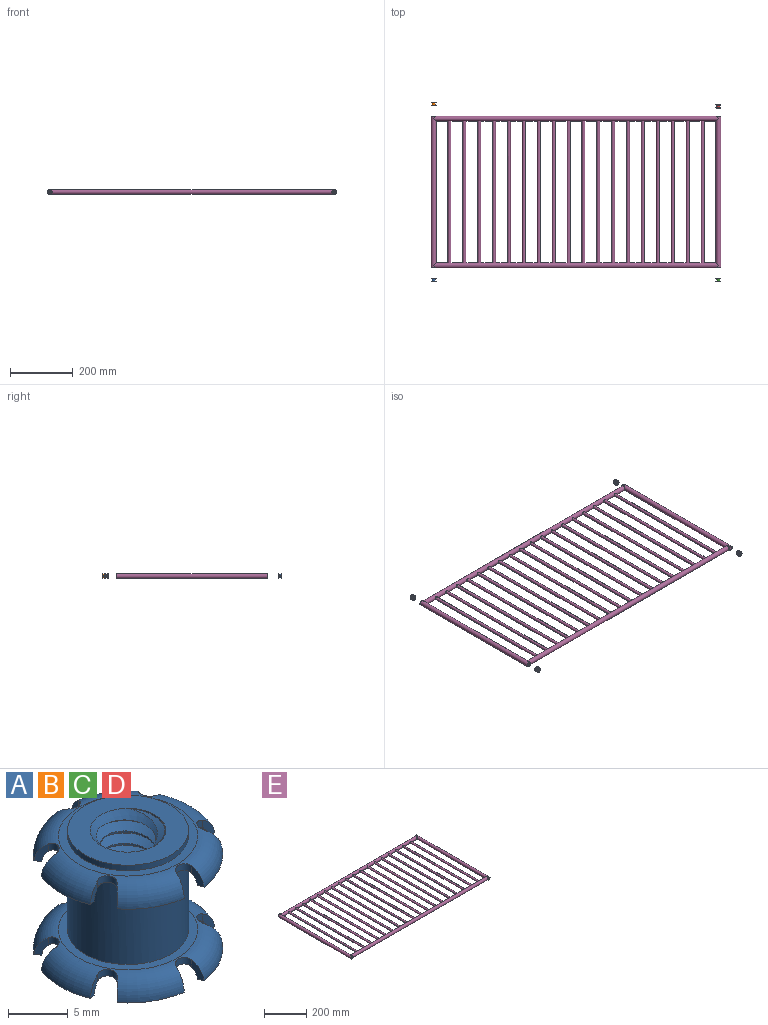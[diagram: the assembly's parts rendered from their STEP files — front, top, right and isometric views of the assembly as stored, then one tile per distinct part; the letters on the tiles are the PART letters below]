
ASSEMBLY  parts=5 mates=4
PART A: 67 faces, bbox 17.3x17.3x12.8 mm
  f0: cylinder r=0.88mm len=1.51mm, axis (0,0,1), area 1.6mm2, adj f8,f9,f65,f66
  f1: cylinder r=0.88mm len=1.51mm, axis (0,0,1), area 1.6mm2, adj f6,f7,f63,f64
  f2: cylinder r=0.88mm len=1.51mm, axis (0,0,1), area 1.6mm2, adj f8,f9,f43,f44
  f3: cylinder r=0.88mm len=1.51mm, axis (0,0,1), area 1.6mm2, adj f6,f7,f41,f42
  f4: cylinder r=0.88mm len=1.7mm, axis (0,0,1), area 1.6mm2, adj f8,f9,f39,f40
  f5: cylinder r=0.88mm len=1.7mm, axis (0,0,1), area 1.6mm2, adj f6,f7,f37,f38
  f6: torus R=5.84mm, axis (0,0,-1), area 71.2mm2, adj f1,f3,f5,f18,f20,f22,f24,f26
  f7: torus R=5.84mm, axis (0,0,-1), area 107.1mm2, adj f1,f3,f5,f18,f20,f22,f24,f26
  f8: torus R=5.84mm, axis (0,0,-1), area 71.2mm2, adj f0,f2,f4,f17,f19,f21,f23,f25
  f9: torus R=5.84mm, axis (0,0,-1), area 107.1mm2, adj f0,f2,f4,f17,f19,f21,f23,f25
  f10: cone r=3.17mm half-angle=45deg, axis (0,0,1), area 10.5mm2, adj f16,f27,f28,f30
  f11: cone r=3.17mm half-angle=45deg, axis (0,0,-1), area 10.5mm2, adj f16,f27,f28,f29
  f12: cylinder r=5.08mm len=10.16mm, axis (0,0,-1), area 18.2mm2, adj f29,f35
  f13: cylinder r=5.08mm len=10.16mm, axis (0,0,-1), area 286.2mm2, adj f32,f34
  f14: cylinder r=5.08mm len=10.16mm, axis (0,0,-1), area 18.2mm2, adj f30,f31
  f15: cylinder r=3.17mm len=11.43mm, axis (0,0,-1), area 28.5mm2, adj f27,f28,f29,f30
  f16: cylinder r=2.35mm len=9.78mm, axis (0,0,-1), area 18mm2, adj f10,f11,f27,f28
  f17: cone r=7.94mm half-angle=85.2deg, axis (0,0,1), area 3.8mm2, adj f8,f9,f62,f65
  f18: cone r=7.94mm half-angle=85.2deg, axis (0,0,1), area 3.8mm2, adj f6,f7,f58,f63
  f19: cone r=7.94mm half-angle=85.2deg, axis (0,0,1), area 3.8mm2, adj f8,f9,f56,f61
  f20: cone r=7.94mm half-angle=85.2deg, axis (0,0,1), area 3.8mm2, adj f6,f7,f52,f57
  f21: cone r=7.94mm half-angle=85.2deg, axis (0,0,1), area 3.8mm2, adj f8,f9,f50,f55
  f22: cone r=7.94mm half-angle=85.2deg, axis (0,0,1), area 3.8mm2, adj f6,f7,f46,f51
  f23: cone r=7.94mm half-angle=85.2deg, axis (0,0,1), area 3.8mm2, adj f8,f9,f44,f49
  f24: cone r=7.94mm half-angle=85.2deg, axis (0,0,1), area 3.8mm2, adj f6,f7,f42,f45
  f25: cone r=7.94mm half-angle=85.2deg, axis (0,0,1), area 3.8mm2, adj f8,f9,f40,f43
  f26: cone r=7.94mm half-angle=85.2deg, axis (0,0,1), area 3.8mm2, adj f6,f7,f38,f41
  f27: bspline ~11.91x7.33mm, area 138.8mm2, adj f10,f11,f15,f16
  f28: bspline ~12.12x7.33mm, area 138.9mm2, adj f10,f11,f15,f16
  f29: plane 10.16x10.16mm, normal (0,0,-1), area 49.4mm2, adj f11,f12,f15
  f30: plane 10.16x10.16mm, normal (0,0,1), area 49.4mm2, adj f10,f14,f15
  f31: plane 11.68x11.68mm, normal (0,0,1), area 26.1mm2, adj f9,f14
  f32: plane 11.68x11.68mm, normal (0,0,-1), area 26.1mm2, adj f8,f13
  f33: cone r=7.94mm half-angle=85.2deg, axis (0,0,1), area 3.8mm2, adj f8,f9,f39,f66
  f34: plane 11.68x11.68mm, normal (0,0,1), area 26.1mm2, adj f7,f13
  f35: plane 11.68x11.68mm, normal (0,0,-1), area 26.1mm2, adj f6,f12
  f36: cone r=7.94mm half-angle=85.2deg, axis (0,0,1), area 3.8mm2, adj f6,f7,f37,f64
  f37: plane 1.86x1.26mm, normal (0.97,0.26,0), area 1.1mm2, adj f5,f6,f7,f36
  f38: plane 1.86x1.26mm, normal (-0.97,0.26,0), area 1.1mm2, adj f5,f6,f7,f26
  f39: plane 1.86x1.26mm, normal (0.97,0.26,0), area 1.1mm2, adj f4,f8,f9,f33
  f40: plane 1.86x1.26mm, normal (-0.97,0.26,0), area 1.1mm2, adj f4,f8,f9,f25
  f41: plane 1.86x0.94mm, normal (0.71,-0.71,0), area 1.1mm2, adj f3,f6,f7,f26
  f42: plane 1.86x1.26mm, normal (-0.26,0.97,0), area 1.1mm2, adj f3,f6,f7,f24
  f43: plane 1.86x0.94mm, normal (0.71,-0.71,0), area 1.1mm2, adj f2,f8,f9,f25
  f44: plane 1.86x1.26mm, normal (-0.26,0.97,0), area 1.1mm2, adj f2,f8,f9,f23
  f45: plane 1.86x1.26mm, normal (-0.26,-0.97,0), area 1.1mm2, adj f6,f7,f24,f47
  f46: plane 1.86x0.94mm, normal (0.71,0.71,0), area 1.1mm2, adj f6,f7,f22,f47
  f47: cylinder r=0.88mm len=1.51mm, axis (0,0,1), area 1.8mm2, adj f6,f7,f45,f46
  f48: cylinder r=0.88mm len=1.51mm, axis (0,0,1), area 1.8mm2, adj f8,f9,f49,f50
  f49: plane 1.86x1.26mm, normal (-0.26,-0.97,0), area 1.1mm2, adj f8,f9,f23,f48
  f50: plane 1.86x0.94mm, normal (0.71,0.71,0), area 1.1mm2, adj f8,f9,f21,f48
  f51: plane 1.86x1.26mm, normal (-0.97,-0.26,0), area 1.1mm2, adj f6,f7,f22,f53
  f52: plane 1.86x1.26mm, normal (0.97,-0.26,0), area 1.1mm2, adj f6,f7,f20,f53
  f53: cylinder r=0.88mm len=1.7mm, axis (0,0,1), area 1.6mm2, adj f6,f7,f51,f52
  f54: cylinder r=0.88mm len=1.7mm, axis (0,0,1), area 1.6mm2, adj f8,f9,f55,f56
  f55: plane 1.86x1.26mm, normal (-0.97,-0.26,0), area 1.1mm2, adj f8,f9,f21,f54
  f56: plane 1.86x1.26mm, normal (0.97,-0.26,0), area 1.1mm2, adj f8,f9,f19,f54
  f57: plane 1.86x0.94mm, normal (-0.71,0.71,0), area 1.1mm2, adj f6,f7,f20,f59
  f58: plane 1.86x1.26mm, normal (0.26,-0.97,0), area 1.1mm2, adj f6,f7,f18,f59
  f59: cylinder r=0.88mm len=1.51mm, axis (0,0,1), area 1.8mm2, adj f6,f7,f57,f58
  f60: cylinder r=0.88mm len=1.51mm, axis (0,0,1), area 1.8mm2, adj f8,f9,f61,f62
  f61: plane 1.86x0.94mm, normal (-0.71,0.71,0), area 1.1mm2, adj f8,f9,f19,f60
  f62: plane 1.86x1.26mm, normal (0.26,-0.97,0), area 1.1mm2, adj f8,f9,f17,f60
  f63: plane 1.86x1.26mm, normal (0.26,0.97,0), area 1.1mm2, adj f1,f6,f7,f18
  f64: plane 1.86x0.94mm, normal (-0.71,-0.71,0), area 1.1mm2, adj f1,f6,f7,f36
  f65: plane 1.86x1.26mm, normal (0.26,0.97,0), area 1.1mm2, adj f0,f8,f9,f17
  f66: plane 1.86x0.94mm, normal (-0.71,-0.71,0), area 1.1mm2, adj f0,f8,f9,f33
PART B: same geometry as A
PART C: same geometry as A
PART D: same geometry as A
PART E: 92 faces, bbox 927.1x485.8x15.9 mm
  f0: cylinder r=7.94mm len=911.23mm, axis (1,0,0), area 43594.6mm2, adj f2,f3,f11,f12,f14,f15,f16,f17
  f1: cylinder r=7.94mm len=911.23mm, axis (1,0,0), area 43590.2mm2, adj f3,f4,f12,f13,f14,f15,f16,f17
  f2: cylinder r=7.94mm len=7.94mm, axis (0,-1,0), area 36mm2, adj f0,f3,f5
  f3: cylinder r=7.94mm len=485.78mm, axis (0,-1,0), area 23651mm2, adj f0,f1,f2,f4,f5,f7
  f4: cylinder r=7.94mm len=7.94mm, axis (0,-1,0), area 36mm2, adj f1,f3,f7
  f5: plane 15.88x15.88mm, normal (0,1,0), area 57.2mm2, adj f2,f3,f6
  f6: cylinder r=6.69mm len=485.78mm, axis (0,-1,0), area 20428.2mm2, adj f5,f7
  f7: plane 15.88x15.88mm, normal (0,-1,0), area 57.2mm2, adj f3,f4,f6
  f8: plane 15.88x15.88mm, normal (0,-1,0), area 57.2mm2, adj f9,f12,f13
  f9: cylinder r=6.69mm len=485.78mm, axis (0,-1,0), area 20428.2mm2, adj f8,f10
  f10: plane 15.88x15.88mm, normal (0,1,0), area 57.2mm2, adj f9,f11,f12
  f11: cylinder r=7.94mm len=7.94mm, axis (0,-1,0), area 36mm2, adj f0,f10,f12
  f12: cylinder r=7.94mm len=485.78mm, axis (0,-1,0), area 23651mm2, adj f0,f1,f8,f10,f11,f13
  f13: cylinder r=7.94mm len=7.94mm, axis (0,-1,0), area 36mm2, adj f1,f8,f12
  f14: cylinder r=4.76mm len=457.2mm, axis (0,-1,0), area 13632.3mm2, adj f0,f1
  f15: cylinder r=4.76mm len=457.2mm, axis (0,-1,0), area 13632.3mm2, adj f0,f1
  f16: cylinder r=4.76mm len=457.2mm, axis (0,-1,0), area 13632.3mm2, adj f0,f1
  f17: cylinder r=4.76mm len=457.2mm, axis (0,-1,0), area 13632.3mm2, adj f0,f1
  f18: cylinder r=4.76mm len=457.2mm, axis (0,-1,0), area 13632.3mm2, adj f0,f1
  f19: cylinder r=4.76mm len=457.2mm, axis (0,-1,0), area 13632.3mm2, adj f0,f1
  f20: cylinder r=4.76mm len=457.2mm, axis (0,-1,0), area 13632.3mm2, adj f0,f1
  f21: cylinder r=4.76mm len=457.2mm, axis (0,-1,0), area 13632.3mm2, adj f0,f1
  f22: cylinder r=4.76mm len=457.2mm, axis (0,-1,0), area 13632.3mm2, adj f0,f1
  f23: cylinder r=4.76mm len=457.2mm, axis (0,-1,0), area 13632.3mm2, adj f0,f1
  f24: cylinder r=4.76mm len=457.2mm, axis (0,-1,0), area 13632.3mm2, adj f0,f1
  f25: cylinder r=4.76mm len=457.2mm, axis (0,-1,0), area 13632.3mm2, adj f0,f1
  f26: cylinder r=4.76mm len=457.2mm, axis (0,-1,0), area 13632.3mm2, adj f0,f1
  f27: cylinder r=4.76mm len=457.2mm, axis (0,-1,0), area 13632.3mm2, adj f0,f1
  f28: cylinder r=4.76mm len=457.2mm, axis (0,-1,0), area 13632.3mm2, adj f0,f1
  f29: cylinder r=4.76mm len=457.2mm, axis (0,-1,0), area 13632.3mm2, adj f0,f1
  f30: cylinder r=4.76mm len=457.2mm, axis (0,-1,0), area 13632.3mm2, adj f0,f1
  f31: cylinder r=4.76mm len=457.2mm, axis (0,-1,0), area 13632.3mm2, adj f0,f1
  f32: cylinder r=3.87mm len=456.04mm, axis (0,-1,0), area 11074.2mm2, adj f33,f34
  f33: cylinder r=7.94mm len=7.75mm, axis (1,0,0), area 48.6mm2, adj f32
  f34: cylinder r=7.94mm len=7.75mm, axis (1,0,0), area 48.7mm2, adj f32
  f35: cylinder r=3.87mm len=456.04mm, axis (0,-1,0), area 11074.2mm2, adj f36,f37
  f36: cylinder r=7.94mm len=7.75mm, axis (1,0,0), area 48.6mm2, adj f35
  f37: cylinder r=7.94mm len=7.75mm, axis (1,0,0), area 48.7mm2, adj f35
  f38: cylinder r=3.87mm len=456.04mm, axis (0,-1,0), area 11074.2mm2, adj f39,f40
  f39: cylinder r=7.94mm len=7.75mm, axis (1,0,0), area 48.6mm2, adj f38
  f40: cylinder r=7.94mm len=7.75mm, axis (1,0,0), area 48.7mm2, adj f38
  f41: cylinder r=3.87mm len=456.04mm, axis (0,-1,0), area 11074.2mm2, adj f42,f43
  f42: cylinder r=7.94mm len=7.75mm, axis (1,0,0), area 48.6mm2, adj f41
  f43: cylinder r=7.94mm len=7.75mm, axis (1,0,0), area 48.7mm2, adj f41
  f44: cylinder r=3.87mm len=456.04mm, axis (0,-1,0), area 11074.2mm2, adj f45,f46
  f45: cylinder r=7.94mm len=7.75mm, axis (1,0,0), area 48.6mm2, adj f44
  f46: cylinder r=7.94mm len=7.75mm, axis (1,0,0), area 48.7mm2, adj f44
  f47: cylinder r=3.87mm len=456.04mm, axis (0,-1,0), area 11074.2mm2, adj f48,f49
  f48: cylinder r=7.94mm len=7.75mm, axis (1,0,0), area 48.6mm2, adj f47
  f49: cylinder r=7.94mm len=7.75mm, axis (1,0,0), area 48.7mm2, adj f47
  f50: cylinder r=3.87mm len=456.04mm, axis (0,-1,0), area 11074.2mm2, adj f51,f52
  f51: cylinder r=7.94mm len=7.75mm, axis (1,0,0), area 48.6mm2, adj f50
  f52: cylinder r=7.94mm len=7.75mm, axis (1,0,0), area 48.7mm2, adj f50
  f53: cylinder r=3.87mm len=456.04mm, axis (0,-1,0), area 11074.2mm2, adj f54,f55
  f54: cylinder r=7.94mm len=7.75mm, axis (1,0,0), area 48.6mm2, adj f53
  f55: cylinder r=7.94mm len=7.75mm, axis (1,0,0), area 48.7mm2, adj f53
  f56: cylinder r=3.87mm len=456.04mm, axis (0,-1,0), area 11074.2mm2, adj f57,f58
  f57: cylinder r=7.94mm len=7.75mm, axis (1,0,0), area 48.6mm2, adj f56
  f58: cylinder r=7.94mm len=7.75mm, axis (1,0,0), area 48.7mm2, adj f56
  f59: cylinder r=3.87mm len=456.04mm, axis (0,-1,0), area 11074.2mm2, adj f60,f61
  f60: cylinder r=7.94mm len=7.75mm, axis (1,0,0), area 48.6mm2, adj f59
  f61: cylinder r=7.94mm len=7.75mm, axis (1,0,0), area 48.7mm2, adj f59
  f62: cylinder r=3.87mm len=456.04mm, axis (0,-1,0), area 11074.2mm2, adj f63,f64
  f63: cylinder r=7.94mm len=7.75mm, axis (1,0,0), area 48.6mm2, adj f62
  f64: cylinder r=7.94mm len=7.75mm, axis (1,0,0), area 48.7mm2, adj f62
  f65: cylinder r=3.87mm len=456.04mm, axis (0,-1,0), area 11074.2mm2, adj f66,f67
  f66: cylinder r=7.94mm len=7.75mm, axis (1,0,0), area 48.6mm2, adj f65
  f67: cylinder r=7.94mm len=7.75mm, axis (1,0,0), area 48.7mm2, adj f65
  f68: cylinder r=3.87mm len=456.04mm, axis (0,-1,0), area 11074.2mm2, adj f69,f70
  f69: cylinder r=7.94mm len=7.75mm, axis (1,0,0), area 48.6mm2, adj f68
  f70: cylinder r=7.94mm len=7.75mm, axis (1,0,0), area 48.7mm2, adj f68
  f71: cylinder r=3.87mm len=456.04mm, axis (0,-1,0), area 11074.2mm2, adj f72,f73
  f72: cylinder r=7.94mm len=7.75mm, axis (1,0,0), area 48.6mm2, adj f71
  f73: cylinder r=7.94mm len=7.75mm, axis (1,0,0), area 48.7mm2, adj f71
  f74: cylinder r=3.87mm len=456.04mm, axis (0,-1,0), area 11074.2mm2, adj f75,f76
  f75: cylinder r=7.94mm len=7.75mm, axis (1,0,0), area 48.6mm2, adj f74
  f76: cylinder r=7.94mm len=7.75mm, axis (1,0,0), area 48.7mm2, adj f74
  f77: cylinder r=3.87mm len=456.04mm, axis (0,-1,0), area 11074.2mm2, adj f78,f79
  f78: cylinder r=7.94mm len=7.75mm, axis (1,0,0), area 48.6mm2, adj f77
  f79: cylinder r=7.94mm len=7.75mm, axis (1,0,0), area 48.7mm2, adj f77
  f80: cylinder r=3.87mm len=456.04mm, axis (0,-1,0), area 11074.2mm2, adj f81,f82
  f81: cylinder r=7.94mm len=7.75mm, axis (1,0,0), area 48.6mm2, adj f80
  f82: cylinder r=7.94mm len=7.75mm, axis (1,0,0), area 48.7mm2, adj f80
  f83: cylinder r=3.87mm len=456.04mm, axis (0,-1,0), area 11074.2mm2, adj f84,f85
  f84: cylinder r=7.94mm len=7.75mm, axis (1,0,0), area 48.6mm2, adj f83
  f85: cylinder r=7.94mm len=7.75mm, axis (1,0,0), area 48.7mm2, adj f83
  f86: cylinder r=7.94mm len=13.39mm, axis (0,-1,0), area 158.8mm2, adj f87
  f87: cylinder r=6.69mm len=902.69mm, axis (1,0,0), area 37794.4mm2, adj f86,f88
  f88: cylinder r=7.94mm len=13.39mm, axis (0,-1,0), area 158.9mm2, adj f87
  f89: cylinder r=7.94mm len=13.39mm, axis (0,-1,0), area 158.9mm2, adj f91
  f90: cylinder r=7.94mm len=13.39mm, axis (0,-1,0), area 158.9mm2, adj f91
  f91: cylinder r=6.69mm len=902.69mm, axis (1,0,0), area 37794.7mm2, adj f89,f90
PLACE A rot(axis=(-0.97,0.18,0.18),92deg) t=(-455.61,-281.07,598.96)mm
PLACE B rot(axis=(0.98,-0.12,0.12),90.9deg) t=(-455.61,281.22,598.96)mm
PLACE C rot(axis=(-0.84,-0.39,-0.39),100deg) t=(455.61,-281.21,598.96)mm
PLACE D rot(axis=(1,0.01,-0.01),90deg) t=(455.61,272.84,598.96)mm
PLACE E at identity fixed
MATE cylindrical C.f6 <-> E.f9  axis (0,-1,0) through (455.61,-285.7,598.96)mm
MATE cylindrical B.f6 <-> E.f2  axis (0,1,0) through (-455.61,285.71,598.96)mm
MATE cylindrical A.f6 <-> E.f2  axis (0,1,0) through (-455.61,-285.55,598.96)mm
MATE cylindrical D.f6 <-> E.f9  axis (0,1,0) through (455.61,278.56,598.96)mm
